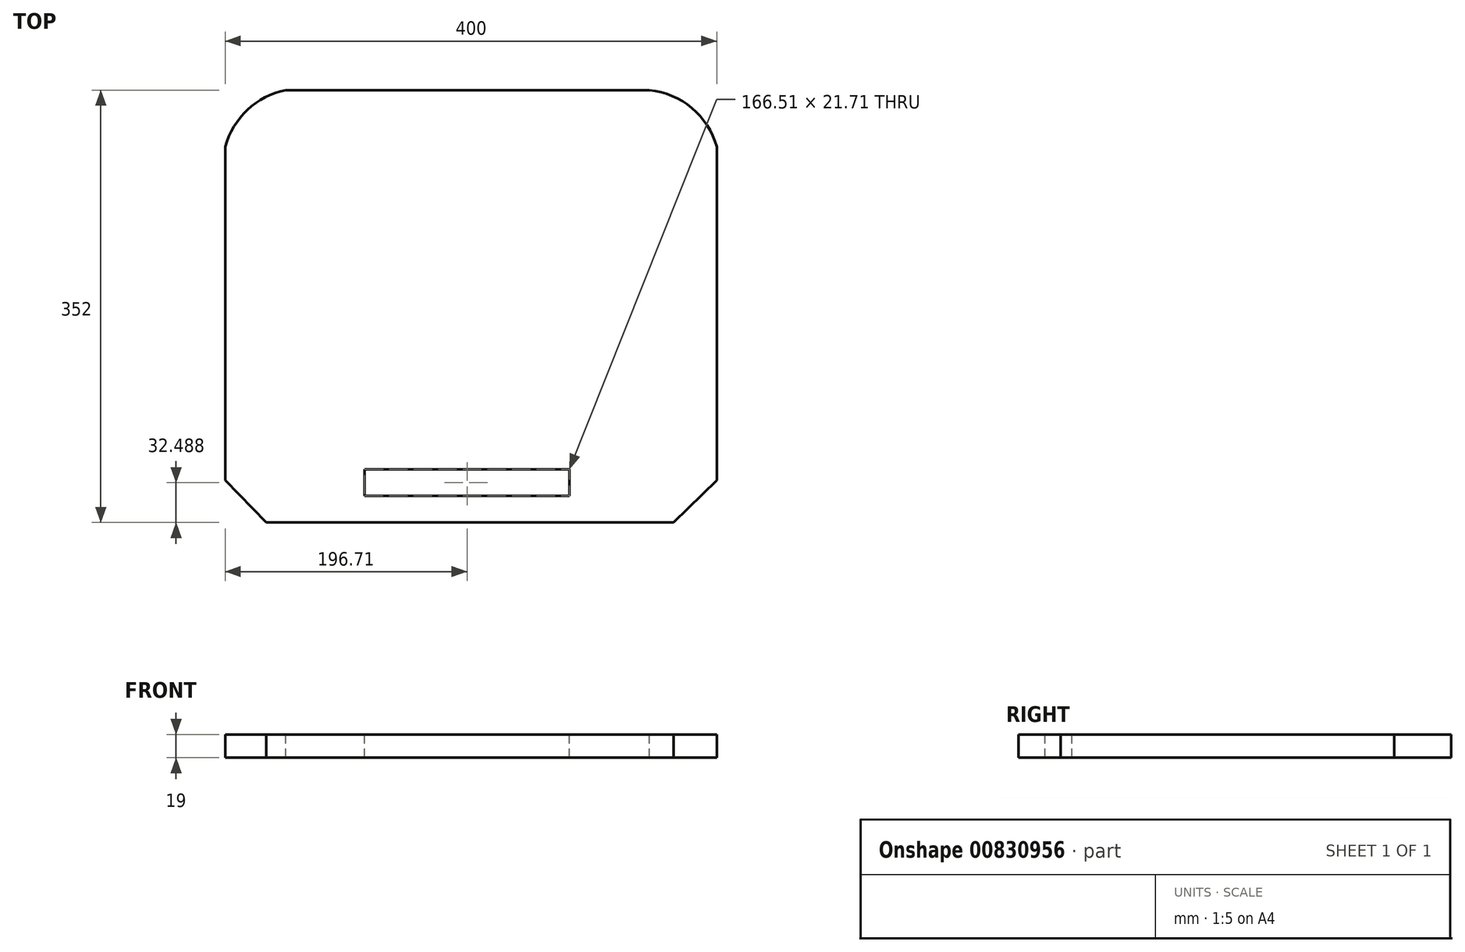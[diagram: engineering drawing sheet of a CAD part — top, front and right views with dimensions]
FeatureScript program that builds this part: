
annotation { "Feature Type Name" : "Feature", "Feature Type Description" : "" }
export const myFeature = defineFeature(function(context is Context, id is Id, definition is map)
    precondition{}
    {
        {
            var Q0;
            Q0=qCreatedBy(makeId("Top.planeOp"),FACE);
            var sketch = newSketch(context, id + "F0", { "sketchPlane" : qUnion([Q0])});
            skLineSegment(sketch, "E0.bottom", {"start": v(203.3, -176) * mm, "end": v(-196.7, -176) * mm});
            skLineSegment(sketch, "E0.top", {"start": v(203.3, 176) * mm, "end": v(-196.7, 176) * mm});
            skLineSegment(sketch, "E0.left", {"start": v(203.3, -176) * mm, "end": v(203.3, 176) * mm});
            skLineSegment(sketch, "E0.right", {"start": v(-196.7, -176) * mm, "end": v(-196.7, 176) * mm});
            skPoint(sketch, "E0.middle", {"position": v(3.3, 0) * mm});
            skSolve(sketch);
        }
        {
            var Q0;
            Q0=makeQuery(id+"F0.imprint","IMPRINT",FACE,{"disambiguationData":[TD([[makeQuery(id+"F0.imprint","IMPRINT",EDGE,{"derivedFrom":sQuery(id+"F0.wireOp",EDGE,"E0.bottom")}),-1.0]])]});
            extrude(context, id + "F1", {"entities" : qUnion([Q0]), "depth" : 19 * mm, "offsetDistance" : 25 * mm});
        }
        {
            var Q0;
            Q0=makeQuery(id+"F1.opExtrude","CAP_FACE",FACE,{"disambiguationData":[OSD([sQuery(id+"F0.wireOp",EDGE,"E0.bottom"),sQuery(id+"F0.wireOp",EDGE,"E0.top"),sQuery(id+"F0.wireOp",EDGE,"E0.left"),sQuery(id+"F0.wireOp",EDGE,"E0.right")])],"isStart":false});
            var sketch = newSketch(context, id + "F2", { "sketchPlane" : qUnion([Q0])});
            skArc(sketch, "E1", {"start": v(-147.4, 176) * mm, "mid": v(-178.6, 159.86) * mm, "end": v(-196.7, 129.75) * mm});
            skArc(sketch, "E2", {"start": v(203.3, 129.75) * mm, "mid": v(182.95, 161.4) * mm, "end": v(148.29, 176) * mm});
            skSolve(sketch);
        }
        {
            var Q0;
            {var subQ0=sQuery(id+"F2.wireOp",EDGE,"E1");Q0=makeQuery(id+"F2.imprint","IMPRINT",FACE,{"disambiguationData":[TD([[makeQuery(id+"F2.imprint","IMPRINT",EDGE,{"derivedFrom":subQ0}),-1.0]])]});}
            var Q1;
            {var subQ0=sQuery(id+"F2.wireOp",EDGE,"E2");Q1=makeQuery(id+"F2.imprint","IMPRINT",FACE,{"disambiguationData":[TD([[makeQuery(id+"F2.imprint","IMPRINT",EDGE,{"derivedFrom":subQ0}),-1.0]])]});}
            extrude(context, id + "F3", {"entities" : qUnion([Q0, Q1]), "operationType" : NewBodyOperationType.REMOVE, "endBound" : BoundingType.THROUGH_ALL, "oppositeDirection" : true, "depth" : 25 * mm, "offsetDistance" : 25 * mm});
        }
        {
            var Q0;
            Q0=makeQuery(id+"F1.opExtrude","CAP_FACE",FACE,{"disambiguationData":[OSD([sQuery(id+"F0.wireOp",EDGE,"E0.bottom"),sQuery(id+"F0.wireOp",EDGE,"E0.top"),sQuery(id+"F0.wireOp",EDGE,"E0.left"),sQuery(id+"F0.wireOp",EDGE,"E0.right")])],"isStart":false});
            var sketch = newSketch(context, id + "F4", { "sketchPlane" : qUnion([Q0])});
            skLineSegment(sketch, "E3", {"start": v(-196.7, -141.64) * mm, "end": v(-163.38, -176) * mm});
            skLineSegment(sketch, "E4", {"start": v(167.97, -176) * mm, "end": v(203.4, -141.64) * mm});
            skSolve(sketch);
        }
        {
            var Q0;
            {var subQ0=sQuery(id+"F4.wireOp",EDGE,"E3");Q0=makeQuery(id+"F4.imprint","IMPRINT",FACE,{"disambiguationData":[TD([[makeQuery(id+"F4.imprint","IMPRINT",EDGE,{"derivedFrom":subQ0}),-1.0]])]});}
            var Q1;
            {var subQ0=sQuery(id+"F4.wireOp",EDGE,"E4");var subQ1=makeQuery(id+"F1.opExtrude","CAP_EDGE",EDGE,{"disambiguationData":[OSD([sQuery(id+"F0.wireOp",EDGE,"E0.bottom")])],"isStart":false});var subQ2=makeQuery(id+"F4.imprint","INTERSECT",VERTEX,{"derivedFrom":[subQ1,subQ0]});Q1=makeQuery(id+"F4.imprint","IMPRINT",FACE,{"disambiguationData":[TD([[makeQuery(id+"F4.imprint","IMPRINT",EDGE,{"disambiguationData":[TD([[subQ2,-1.0]])],"derivedFrom":subQ0}),-1.0]])]});}
            extrude(context, id + "F5", {"entities" : qUnion([Q0, Q1]), "operationType" : NewBodyOperationType.REMOVE, "endBound" : BoundingType.THROUGH_ALL, "oppositeDirection" : true, "depth" : 25 * mm, "offsetDistance" : 25 * mm});
        }
        {
            var Q0;
            Q0=makeQuery(id+"F1.opExtrude","CAP_FACE",FACE,{"disambiguationData":[OSD([sQuery(id+"F0.wireOp",EDGE,"E0.bottom"),sQuery(id+"F0.wireOp",EDGE,"E0.top"),sQuery(id+"F0.wireOp",EDGE,"E0.left"),sQuery(id+"F0.wireOp",EDGE,"E0.right")])],"isStart":false});
            var sketch = newSketch(context, id + "F6", { "sketchPlane" : qUnion([Q0])});
            skLineSegment(sketch, "E5.bottom", {"start": v(-83.26, -132.66) * mm, "end": v(83.26, -132.66) * mm});
            skLineSegment(sketch, "E5.top", {"start": v(-83.26, -154.37) * mm, "end": v(83.26, -154.37) * mm});
            skLineSegment(sketch, "E5.left", {"start": v(-83.26, -132.66) * mm, "end": v(-83.26, -154.37) * mm});
            skLineSegment(sketch, "E5.right", {"start": v(83.26, -132.66) * mm, "end": v(83.26, -154.37) * mm});
            skPoint(sketch, "E5.middle", {"position": v(0, -143.51) * mm});
            skSolve(sketch);
        }
        {
            var Q0;
            Q0=makeQuery(id+"F6.imprint","IMPRINT",FACE,{"disambiguationData":[TD([[makeQuery(id+"F6.imprint","IMPRINT",EDGE,{"derivedFrom":sQuery(id+"F6.wireOp",EDGE,"E5.bottom")}),-1.0]])]});
            extrude(context, id + "F7", {"entities" : qUnion([Q0]), "operationType" : NewBodyOperationType.REMOVE, "endBound" : BoundingType.THROUGH_ALL, "oppositeDirection" : true, "depth" : 25 * mm, "offsetDistance" : 25 * mm});
        }
    });
